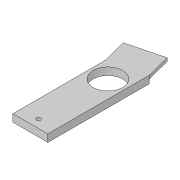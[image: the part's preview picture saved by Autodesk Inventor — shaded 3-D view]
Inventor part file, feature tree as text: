
AUTODESK INVENTOR PART (.ipt)
format: ipt  version: 2018.3 (Build 223284000, 284)  size: 119,296 bytes
history: native  units: in
note: dims shown in document units (in); Inventor stores cm internally (conversion verified against a paired STEP export)
features: extrude x3, sketch x3
ambient origin geometry x8: Origin, YZ Plane, XZ Plane, XY Plane, X Axis, Y Axis, Z Axis, Center Point
bodies: Solid1 (feature_tree)
feature tree (6):
  extrude  "Extrusion1"  Depth=0.221in TaperAngle=0.0deg
  extrude  "Extrusion4"  Depth=0.75in
  extrude  "Extrusion5"  Depth=0.125in
  sketch  "Sketch1"  dims[d4=0.88in d5=0.221in d6=0.0in]
  sketch  "Sketch4"  dims[d30=0.75in d32=0.75in]
  sketch  "Sketch5"  dims[d33=1.0429in d35=0.5215in d36=2.3125in d37=2.75in d38=0.126in d39=0.25in d40=1.0in d41=0.0in d42=0.52in d46=0.119in d47=0.1105in d48=0.125in d49=0.0in]
